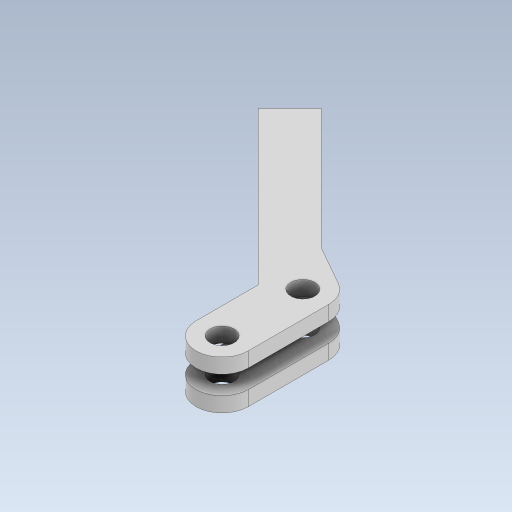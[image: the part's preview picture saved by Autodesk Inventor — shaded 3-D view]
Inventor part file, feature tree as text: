
AUTODESK INVENTOR PART (.ipt)
format: ipt  version: 2023 (Build 270158000, 158)  size: 384,512 bytes
history: native  units: in
note: dims shown in document units (in); Inventor stores cm internally (conversion verified against a paired STEP export)
features: extrude x2, fillet x2, mirror x1, projected_geometry x1
ambient origin geometry x8: Origin, YZ Plane, XZ Plane, XY Plane, X Axis, Y Axis, Z Axis, Center Point
bodies: Solid1 (feature_tree)
feature tree (6):
  extrude  "Extrusion1"  Depth=0.2559in
  fillet  "Fillet1"  Radius=0.8543in
  extrude  "Extrusion4"  Depth=0.2756in
  mirror  "Mirror3"
  fillet  "Fillet3"  Radius=0.2756in
  projected_geometry  "Projected Loop1"
